# Revit family: Samourai S - RHMA 4-7 AVN_
name_source: partatom
category: Mechanical Equipment
revit_build: Autodesk Revit 2018 (Build: 20170223_1515(x64)
units: mm (PartAtom-declared; Revit-internal decimal feet)

## family parameters
Always vertical = Yes
Cut with Voids When Loaded = No
OmniClass Number = 23.75.10.00
OmniClass Title = Transformation and Conversion of Energy
Part Type = Normal
Room Calculation Point = No
Round Connector Dimension = Use Diameter
Shared = No
Work Plane-Based = No

## types (4) — shared parameters
Airflow (High) = 1833.3 L/s
Airflow (Low) = 694.4 L/s
BC_OBJECT_ID = 41993
BC_OBJECT_VERSION = #7
Description = Samurai S - Heat Pump Inverter Scroll. RHMA 4AVN - RHMA 7AVN
Frequency = 50 Hz
Inlet Water Diameter = 25 mm  [stored 0.082021 ft]
Manufacturer = Hitachi Air Conditioning Europe SAS
MasterFormat = Central HVAC Equipment
Masterformat Code = 23 70 00
Model = Samurai S - Heat Pump Inverter Scroll
Name BIM&CO = Chiller
Nominal Voltage = 230 V
Number of Poles = 1
OMNICLASS Table 23 Code  = 23-33 21 13
OmniClass name = Chillers
Operating mode = Heating+Cooling
Overall Height = 1320 mm  [stored 4.33071 ft]
Overall Length = 995 mm
Overall Width = 360 mm
Refrigerant Type = R410A
Starting current = 10 A
Uniformat = Cooling Generating Systems
Uniformat code = D3030
Water Outlet Diameter = 25 mm  [stored 0.082021 ft]

## per-type parameters (varying)
| type | BC_VARIANT_ID | Coefficient of Performance (COP) | Cooling Capacity | Cooling Input Rated | Energy efficiency SCOP | Energy efficiency ratio (EER) | Heating Capacity | Heating Input Rated | Load of Refrigerant Fluid | Packing Weight | Rated Cooling Current | SEER energy efficiency | Sound Power (Cooling) | Sound Power (Heating) | Sound Power Low Noise (Cooling) | Sound Power Low Noise (Heating) | Sound Pressure at 10m (Cooling) | Sound Pressure at 1m (Cooling) | Weight in operation |
| RHMA 4AVN | 259273 | 3 | 11200 W | 4000 W | 3.47 | 2.79 | 10900 W | 3700 W | 2.80 kg | 136.00 kg | 17 A | 4.05 | 68 | 69 | 64 | 66 | 40 | 54 | 126.00 kg |
| RHMA 5AVN | 259274 | 3.06 | 14300 W | 5300 W | 3.55 | 2.7 | 13100 W | 4300 W | 3.30 kg | 138.00 kg | 24 A | 4.32 | 70 | 71 | 65 | 67 | 42 | 55 | 128.00 kg |
| RHMA 6AVN | 259275 | 3.29 | 16000 W | 5700 W | 4.02 | 2.78 | 15400 W | 4700 W | 3.90 kg | 151.00 kg | 26 A | 4.52 | 70 | 71 | 65 | 67 | 42 | 55 | 141.00 kg |
| RHMA 7AVN | 259276 | 2.94 | 17800 W | 6900 W | 3.9 | 2.56 | 18500 W | 6300 W | 4.00 kg | 151.00 kg | 31 A | 4.42 | 74 | 74 | 69 | 70 | 46 | 59 | 141.00 kg |

note: column(s) folded — value = type name in every type: Product Code, Reference, Type Comments

note: [stored X ft] marks values corroborated as IEEE doubles in the binary element streams (Revit-internal decimal feet)
